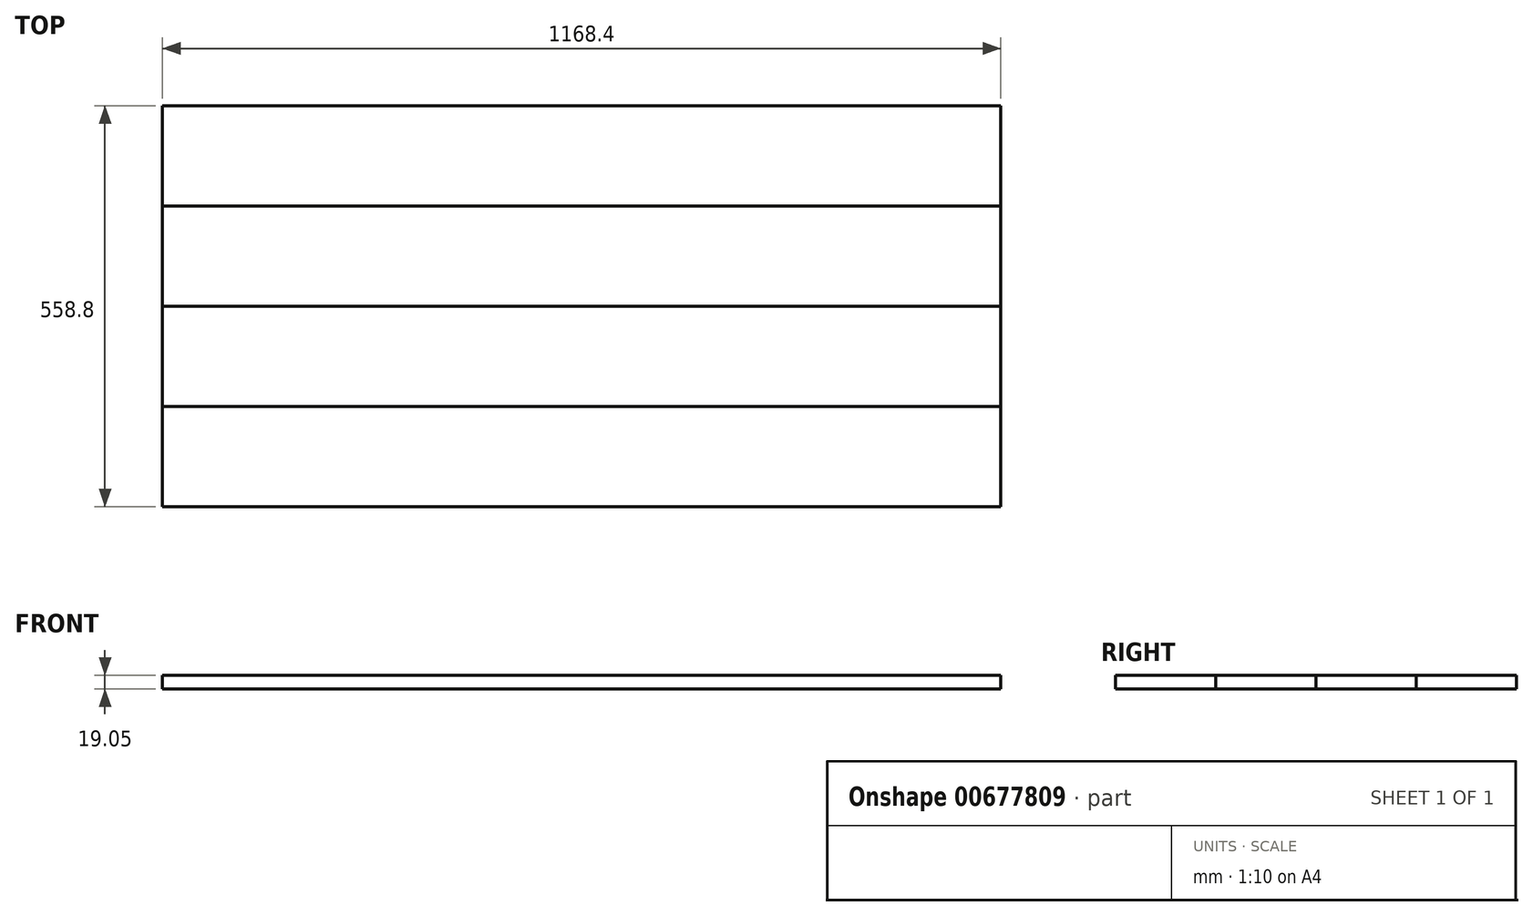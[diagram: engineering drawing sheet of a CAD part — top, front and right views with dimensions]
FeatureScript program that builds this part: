
annotation { "Feature Type Name" : "Feature", "Feature Type Description" : "" }
export const myFeature = defineFeature(function(context is Context, id is Id, definition is map)
    precondition{}
    {
        {
            var Q0;
            Q0=qCreatedBy(makeId("Top.planeOp"),FACE);
            var sketch = newSketch(context, id + "F0", { "sketchPlane" : qUnion([Q0])});
            skLineSegment(sketch, "E0.bottom", {"start": v(-41.48, 150.13) * mm, "end": v(1126.92, 150.13) * mm});
            skLineSegment(sketch, "E0.top", {"start": v(-41.48, 10.43) * mm, "end": v(1126.92, 10.43) * mm});
            skLineSegment(sketch, "E0.left", {"start": v(-41.48, 150.13) * mm, "end": v(-41.48, 10.43) * mm});
            skLineSegment(sketch, "E0.right", {"start": v(1126.92, 150.13) * mm, "end": v(1126.92, 10.43) * mm});
            skSolve(sketch);
        }
        {
            var Q0;
            Q0 = qSketchRegion(id + "F0", true);
            extrude(context, id + "F1", {"entities" : qUnion([Q0]), "depth" : 19.05 * mm, "offsetDistance" : 25.4 * mm});
        }
        {
            var Q0;
            Q0=makeQuery(id+"F1.opExtrude","SWEPT_BODY",BODY,{"disambiguationData":[OSD([sQuery(id+"F0.wireOp",EDGE,"E0.bottom"),sQuery(id+"F0.wireOp",EDGE,"E0.top"),sQuery(id+"F0.wireOp",EDGE,"E0.left"),sQuery(id+"F0.wireOp",EDGE,"E0.right")])]});
            transform(context, id + "F2", {"entities" : qUnion([Q0]), "transformType" : TransformType.TRANSLATION_3D, "dx" : 0 * mm, "dy" : 139.7 * mm, "dz" : 0 * mm, "makeCopy" : true});
        }
        {
            var Q0;
            Q0=makeQuery(id+"F2.opPattern","COPY",BODY,{"derivedFrom":makeQuery(id+"F1.opExtrude","SWEPT_BODY",BODY,{"disambiguationData":[OSD([sQuery(id+"F0.wireOp",EDGE,"E0.bottom"),sQuery(id+"F0.wireOp",EDGE,"E0.top"),sQuery(id+"F0.wireOp",EDGE,"E0.left"),sQuery(id+"F0.wireOp",EDGE,"E0.right")])]}),"instanceName":"1"});
            transform(context, id + "F3", {"entities" : qUnion([Q0]), "transformType" : TransformType.TRANSLATION_3D, "dx" : 0 * mm, "dy" : 139.7 * mm, "dz" : 0 * mm, "makeCopy" : true});
        }
        {
            var Q0;
            Q0=makeQuery(id+"F3.opPattern","COPY",BODY,{"derivedFrom":makeQuery(id+"F2.opPattern","COPY",BODY,{"derivedFrom":makeQuery(id+"F1.opExtrude","SWEPT_BODY",BODY,{"disambiguationData":[OSD([sQuery(id+"F0.wireOp",EDGE,"E0.bottom"),sQuery(id+"F0.wireOp",EDGE,"E0.top"),sQuery(id+"F0.wireOp",EDGE,"E0.left"),sQuery(id+"F0.wireOp",EDGE,"E0.right")])]}),"instanceName":"1"}),"instanceName":"1"});
            transform(context, id + "F4", {"entities" : qUnion([Q0]), "transformType" : TransformType.TRANSLATION_3D, "dx" : 0 * mm, "dy" : 139.7 * mm, "dz" : 0 * mm, "makeCopy" : true});
        }
    });
